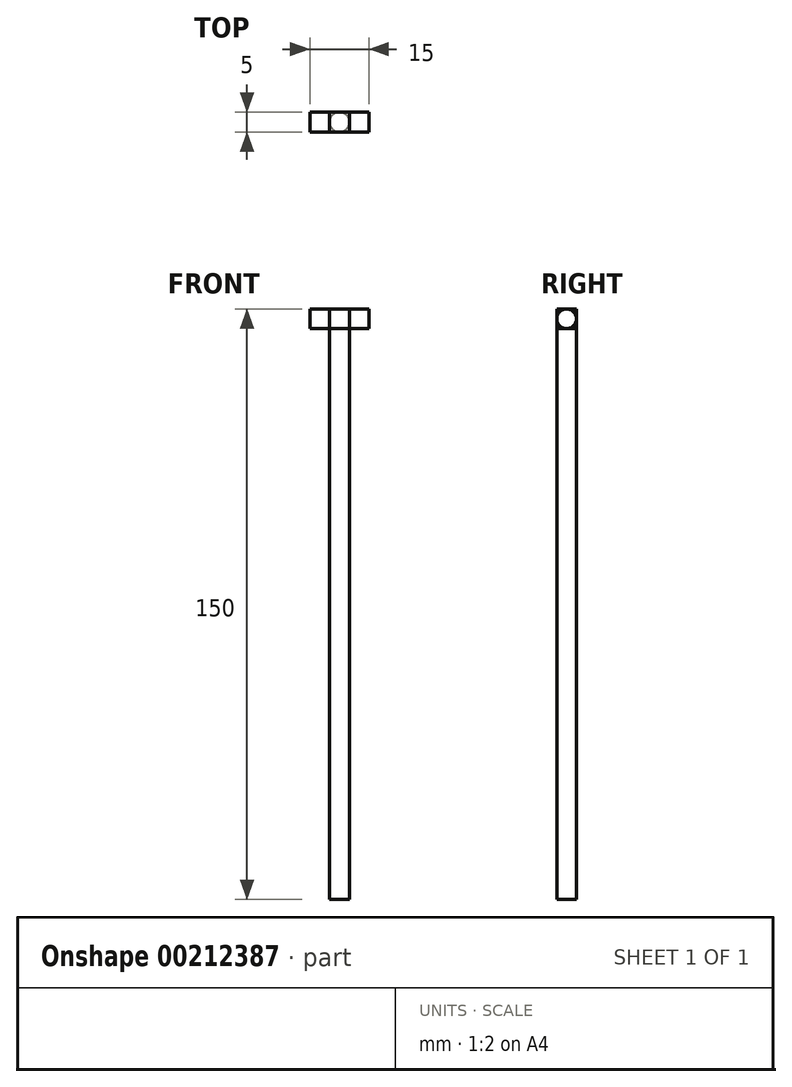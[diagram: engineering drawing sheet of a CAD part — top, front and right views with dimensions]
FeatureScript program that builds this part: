
annotation { "Feature Type Name" : "Feature", "Feature Type Description" : "" }
export const myFeature = defineFeature(function(context is Context, id is Id, definition is map)
    precondition{}
    {
        {
            var Q0;
            Q0=qCreatedBy(makeId("Top.planeOp"),FACE);
            var sketch = newSketch(context, id + "F0", { "sketchPlane" : qUnion([Q0])});
            skCircle(sketch, "E0", {"center": v(0, 0) * mm, "radius": 2.5 * mm});
            skSolve(sketch);
        }
        {
            var Q0;
            Q0=makeQuery(id+"F0.imprint","IMPRINT",FACE,{"disambiguationData":[TD([[makeQuery(id+"F0.imprint","IMPRINT",EDGE,{"derivedFrom":sQuery(id+"F0.wireOp",EDGE,"E0")}),1.0]])]});
            var Q1;
            Q1=sQuery(id+"F0.wireOp",EDGE,"E0");
            extrude(context, id + "F1", {"entities" : qUnion([Q0]), "surfaceEntities" : qUnion([Q1]), "depth" : 145 * mm});
        }
        {
            var Q0;
            Q0=makeQuery(id+"F1.opExtrude","CAP_FACE",FACE,{"disambiguationData":[OSD([sQuery(id+"F0.wireOp",EDGE,"E0")])],"isStart":false});
            var sketch = newSketch(context, id + "F2", { "sketchPlane" : qUnion([Q0])});
            skLineSegment(sketch, "E1.bottom", {"start": v(-2.5, 2.5) * mm, "end": v(2.5, 2.5) * mm});
            skLineSegment(sketch, "E1.top", {"start": v(-2.5, -2.5) * mm, "end": v(2.5, -2.5) * mm});
            skLineSegment(sketch, "E1.left", {"start": v(-2.5, 2.5) * mm, "end": v(-2.5, -2.5) * mm});
            skLineSegment(sketch, "E1.right", {"start": v(2.5, 2.5) * mm, "end": v(2.5, -2.5) * mm});
            skPoint(sketch, "E1.middle", {"position": v(0, 0) * mm});
            skSolve(sketch);
        }
        {
            var Q0;
            {var subQ0=sQuery(id+"F2.wireOp",EDGE,"E1.right");Q0=makeQuery(id+"F2.imprint","IMPRINT",FACE,{"disambiguationData":[TD([[makeQuery(id+"F2.imprint","IMPRINT",EDGE,{"derivedFrom":subQ0}),-1.0]])]});}
            var Q1;
            {var subQ0=makeQuery(id+"F1.opExtrude","CAP_EDGE",EDGE,{"disambiguationData":[OSD([sQuery(id+"F0.wireOp",EDGE,"E0")])],"isStart":false});var subQ1=makeQuery(id+"F2.imprint","INTERSECT",VERTEX,{"derivedFrom":[subQ0,sQuery(id+"F2.wireOp",EDGE,"E1.bottom")]});Q1=makeQuery(id+"F2.imprint","IMPRINT",FACE,{"disambiguationData":[TD([[makeQuery(id+"F2.imprint","IMPRINT",EDGE,{"disambiguationData":[TD([[subQ1,-1.0]])],"derivedFrom":subQ0}),1.0]])]});}
            var Q2;
            {var subQ0=sQuery(id+"F2.wireOp",EDGE,"E1.left");Q2=makeQuery(id+"F2.imprint","IMPRINT",FACE,{"disambiguationData":[TD([[makeQuery(id+"F2.imprint","IMPRINT",EDGE,{"derivedFrom":subQ0}),1.0]])]});}
            extrude(context, id + "F3", {"entities" : qUnion([Q0, Q1, Q2]), "operationType" : NewBodyOperationType.ADD, "depth" : 5 * mm});
        }
        {
            var Q0;
            Q0=makeQuery(id+"F3.opExtrude","SWEPT_FACE",FACE,{"disambiguationData":[OSD([sQuery(id+"F2.wireOp",EDGE,"E1.left")])]});
            var sketch = newSketch(context, id + "F4", { "sketchPlane" : qUnion([Q0])});
            skCircle(sketch, "E2", {"center": v(0, 147.5) * mm, "radius": 2.5 * mm});
            skSolve(sketch);
        }
        {
            var Q0;
            {var subQ0=sQuery(id+"F4.wireOp",EDGE,"E2");var subQ1=sQuery(id+"F2.wireOp",EDGE,"E1.left");var subQ2=makeQuery(id+"F4.imprint","INTERSECT",VERTEX,{"derivedFrom":[makeQuery(id+"F3.opExtrude","CAP_EDGE",EDGE,{"disambiguationData":[OSD([subQ1])],"isStart":false}),subQ0]});Q0=makeQuery(id+"F4.imprint","IMPRINT",FACE,{"disambiguationData":[TD([[makeQuery(id+"F4.imprint","IMPRINT",EDGE,{"disambiguationData":[TD([[subQ2,1.0]])],"derivedFrom":subQ0}),1.0]])]});}
            extrude(context, id + "F5", {"entities" : qUnion([Q0]), "operationType" : NewBodyOperationType.ADD, "depth" : 5 * mm});
        }
        {
            var Q0;
            Q0=makeQuery(id+"F3.opExtrude","SWEPT_FACE",FACE,{"disambiguationData":[OSD([sQuery(id+"F2.wireOp",EDGE,"E1.right")])]});
            var sketch = newSketch(context, id + "F6", { "sketchPlane" : qUnion([Q0])});
            skCircle(sketch, "E3", {"center": v(0, 147.5) * mm, "radius": 2.5 * mm});
            skSolve(sketch);
        }
        {
            var Q0;
            {var subQ0=sQuery(id+"F6.wireOp",EDGE,"E3");var subQ1=sQuery(id+"F2.wireOp",EDGE,"E1.right");var subQ2=makeQuery(id+"F6.imprint","INTERSECT",VERTEX,{"derivedFrom":[makeQuery(id+"F3.opExtrude","CAP_EDGE",EDGE,{"disambiguationData":[OSD([subQ1])],"isStart":false}),subQ0]});Q0=makeQuery(id+"F6.imprint","IMPRINT",FACE,{"disambiguationData":[TD([[makeQuery(id+"F6.imprint","IMPRINT",EDGE,{"disambiguationData":[TD([[subQ2,1.0]])],"derivedFrom":subQ0}),1.0]])]});}
            extrude(context, id + "F7", {"entities" : qUnion([Q0]), "operationType" : NewBodyOperationType.ADD, "depth" : 5 * mm});
        }
    });
